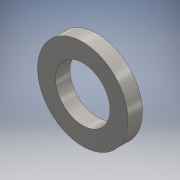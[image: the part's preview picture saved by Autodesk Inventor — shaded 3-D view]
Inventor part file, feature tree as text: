
AUTODESK INVENTOR PART (.ipt)
format: ipt  version: 2016 (Build 200138000, 138)  size: 115,712 bytes
history: native  units: mm
features: extrude x1, sketch x1
ambient origin geometry x8: Origin, YZ Plane, XZ Plane, XY Plane, X Axis, Y Axis, Z Axis, Center Point
bodies: Solid1 (feature_tree)
feature tree (2):
  extrude  "Extrusion1"  Depth=10.0mm
  sketch  "Sketch1"  dims[d0=6.0mm d1=10.0mm d2=1.6mm d3=0.0mm]
